# Revit family: Sanitary_Hand-Hair-Dryers_JVD_JVD-COPT-AIR-HAND-DRYERS_
name_source: partatom
category: Specialty Equipment
units: mm (PartAtom-declared; Revit-internal decimal feet)

## family parameters
Cut with Voids When Loaded = No
Host = Face
OmniClass Number = 23.31.25.15
OmniClass Title = Hand Dryers
Part Type = Normal
Room Calculation Point = No
Round Connector Dimension = Use Diameter
Shared = No

## types (3) — shared parameters
Air outlet temperature (°C) = 40
Apparent Load = 600 VA
Connector Description = Electrical Connection. Exist in 110-120 V (US)
Current = 1 A
Depth = 196 mm  [stored 0.643045 ft]
Description = COPT'AIR hand dryer with low power consumption and anti-vandalism (aluminum cover). Ultra fast drying with its rotating nozzle. Designed for intensive use.
Detection type = Infrared
Drying time (s) = 10-15s
Drying zone lighting = Yes
Filter = Anti-bacterial filter (Option)
Frequency (Hz) = 50
Height = 285 mm  [stored 0.935039 ft]
Manufacturer = JVD
Material = Aluminum
Model = COPT’AIR
Motor lifetime (number of operations) = 350000
Motor speed (rpm) = 24000
Number of Poles = 1
Outlet air speed (m/s) = 90
Power Factor = 1
Product data url = https://bimobject.com
Safety in case of malfunction = Yes
Sound level (dB) (1m in front of the appliance) = 80
Standby power consumption (W) = 2.2000
Type of motor = Brushed AC
URL = www.jvd.fr/en/
Vandal-safe = Yes
Voltage = 230 V
Weight = 4.36 kg
Width = 232 mm  [stored 0.761155 ft]
zero-valued in all types: Default Elevation, Edition number, Version

## per-type parameters (varying)
| type | Colour |
| 8111167 COPT'AIR White | JVD - Plastic - White - RAL 9016 |
| 8111168 COPT'AIR Metallic Gray | JVD - Plastic - Metallic Gray - RAL 9006 |
| 8111377 COPT'AIR Matte Black | JVD - Plastic - Matte Black - RAL 9005 |

note: [stored X ft] marks values corroborated as IEEE doubles in the binary element streams (Revit-internal decimal feet)

## geometry (parser evidence)
native form markers: Sweep x2
no freeform markers — native parametric forms only
